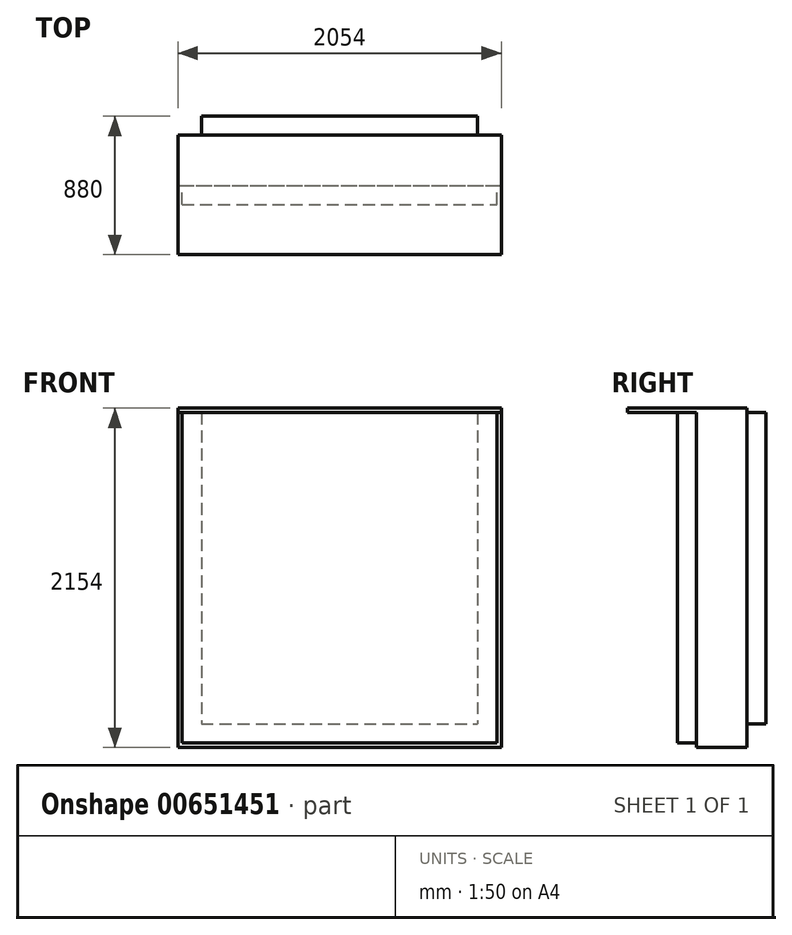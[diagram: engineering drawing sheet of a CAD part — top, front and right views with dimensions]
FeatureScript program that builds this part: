
annotation { "Feature Type Name" : "Feature", "Feature Type Description" : "" }
export const myFeature = defineFeature(function(context is Context, id is Id, definition is map)
    precondition{}
    {
        {
            var Q0;
            Q0=qCreatedBy(makeId("Front.planeOp"),FACE);
            var sketch = newSketch(context, id + "F0", { "sketchPlane" : qUnion([Q0])});
            skLineSegment(sketch, "E0.bottom", {"start": v(1935, 1905) * mm, "end": v(-1935, 1905) * mm});
            skLineSegment(sketch, "E0.top", {"start": v(1935, -1905) * mm, "end": v(-1935, -1905) * mm});
            skLineSegment(sketch, "E0.left", {"start": v(1935, 1905) * mm, "end": v(1935, -1905) * mm});
            skLineSegment(sketch, "E0.right", {"start": v(-1935, 1905) * mm, "end": v(-1935, -1905) * mm});
            skPoint(sketch, "E0.middle", {"position": v(0, 0) * mm});
            skSolve(sketch);
        }
        {
            var Q0;
            Q0=makeQuery(id+"F0.imprint","IMPRINT",FACE,{"disambiguationData":[TD([[makeQuery(id+"F0.imprint","IMPRINT",EDGE,{"derivedFrom":sQuery(id+"F0.wireOp",EDGE,"E0.bottom")}),1.0]])]});
            var sketch = newSketch(context, id + "F1", { "sketchPlane" : qUnion([Q0])});
            skLineSegment(sketch, "E1.bottom", {"start": v(-877, 1878) * mm, "end": v(877, 1878) * mm});
            skLineSegment(sketch, "E1.top", {"start": v(-877, -99) * mm, "end": v(877, -99) * mm});
            skLineSegment(sketch, "E1.left", {"start": v(-877, 1878) * mm, "end": v(-877, -99) * mm});
            skLineSegment(sketch, "E1.right", {"start": v(877, 1878) * mm, "end": v(877, -99) * mm});
            skSolve(sketch);
        }
        {
            var Q0;
            Q0=makeQuery(id+"F1.imprint","IMPRINT",FACE,{"disambiguationData":[TD([[makeQuery(id+"F1.imprint","IMPRINT",EDGE,{"derivedFrom":sQuery(id+"F1.wireOp",EDGE,"E1.bottom")}),-1.0]])]});
            extrude(context, id + "F2", {"entities" : qUnion([Q0]), "depth" : 120 * mm, "offsetDistance" : 25 * mm});
        }
        {
            var Q0;
            Q0=makeQuery(id+"F2.opExtrude","CAP_FACE",FACE,{"disambiguationData":[OSD([sQuery(id+"F1.wireOp",EDGE,"E1.bottom"),sQuery(id+"F1.wireOp",EDGE,"E1.top"),sQuery(id+"F1.wireOp",EDGE,"E1.left"),sQuery(id+"F1.wireOp",EDGE,"E1.right")])],"isStart":false});
            var sketch = newSketch(context, id + "F3", { "sketchPlane" : qUnion([Q0])});
            skLineSegment(sketch, "E2.bottom", {"start": v(-1027, 1905) * mm, "end": v(1027, 1905) * mm});
            skLineSegment(sketch, "E2.top", {"start": v(-1027, -249) * mm, "end": v(1027, -249) * mm});
            skLineSegment(sketch, "E2.left", {"start": v(-1027, 1905) * mm, "end": v(-1027, -249) * mm});
            skLineSegment(sketch, "E2.right", {"start": v(1027, 1905) * mm, "end": v(1027, -249) * mm});
            skSolve(sketch);
        }
        {
            var Q0;
            Q0=makeQuery(id+"F3.imprint","IMPRINT",FACE,{"disambiguationData":[TD([[makeQuery(id+"F3.imprint","IMPRINT",EDGE,{"derivedFrom":makeQuery(id+"F2.opExtrude","CAP_EDGE",EDGE,{"disambiguationData":[OSD([sQuery(id+"F1.wireOp",EDGE,"E1.bottom")])],"isStart":false})}),-1.0]])]});
            var Q1;
            Q1=makeQuery(id+"F3.imprint","IMPRINT",FACE,{"disambiguationData":[TD([[makeQuery(id+"F3.imprint","IMPRINT",EDGE,{"derivedFrom":sQuery(id+"F3.wireOp",EDGE,"E2.bottom")}),-1.0]])]});
            extrude(context, id + "F4", {"entities" : qUnion([Q0, Q1]), "operationType" : NewBodyOperationType.ADD, "depth" : 320 * mm, "offsetDistance" : 25 * mm});
        }
        {
            var Q0;
            Q0=makeQuery(id+"F4.opExtrude","CAP_FACE",FACE,{"disambiguationData":[OSD([sQuery(id+"F3.wireOp",EDGE,"E2.bottom"),sQuery(id+"F3.wireOp",EDGE,"E2.top"),sQuery(id+"F3.wireOp",EDGE,"E2.left"),sQuery(id+"F3.wireOp",EDGE,"E2.right")])],"isStart":false});
            var sketch = newSketch(context, id + "F5", { "sketchPlane" : qUnion([Q0])});
            skLineSegment(sketch, "E3.bottom", {"start": v(-1027, 1905) * mm, "end": v(1027, 1905) * mm});
            skLineSegment(sketch, "E3.top", {"start": v(-1027, 1878) * mm, "end": v(1027, 1878) * mm});
            skLineSegment(sketch, "E3.left", {"start": v(-1027, 1905) * mm, "end": v(-1027, 1878) * mm});
            skLineSegment(sketch, "E3.right", {"start": v(1027, 1905) * mm, "end": v(1027, 1878) * mm});
            skLineSegment(sketch, "E4.bottom", {"start": v(-1000, -222) * mm, "end": v(1000, -222) * mm});
            skLineSegment(sketch, "E4.top", {"start": v(-1000, 1878) * mm, "end": v(1000, 1878) * mm});
            skLineSegment(sketch, "E4.left", {"start": v(-1000, -222) * mm, "end": v(-1000, 1878) * mm});
            skLineSegment(sketch, "E4.right", {"start": v(1000, -222) * mm, "end": v(1000, 1878) * mm});
            skSolve(sketch);
        }
        {
            var Q0;
            Q0=makeQuery(id+"F5.imprint","IMPRINT",FACE,{"disambiguationData":[TD([[makeQuery(id+"F5.imprint","IMPRINT",EDGE,{"derivedFrom":sQuery(id+"F5.wireOp",EDGE,"E4.bottom")}),1.0]])]});
            extrude(context, id + "F6", {"entities" : qUnion([Q0]), "operationType" : NewBodyOperationType.ADD, "depth" : 120 * mm, "offsetDistance" : 25 * mm});
        }
        {
            var Q0;
            Q0=makeQuery(id+"F4.opExtrude","CAP_FACE",FACE,{"disambiguationData":[OSD([sQuery(id+"F3.wireOp",EDGE,"E2.bottom"),sQuery(id+"F3.wireOp",EDGE,"E2.top"),sQuery(id+"F3.wireOp",EDGE,"E2.left"),sQuery(id+"F3.wireOp",EDGE,"E2.right")])],"isStart":false});
            var sketch = newSketch(context, id + "F7", { "sketchPlane" : qUnion([Q0])});
            skLineSegment(sketch, "E5.bottom", {"start": v(-1027, 1905) * mm, "end": v(1027, 1905) * mm});
            skLineSegment(sketch, "E5.top", {"start": v(-1027, 1878) * mm, "end": v(1027, 1878) * mm});
            skLineSegment(sketch, "E5.left", {"start": v(-1027, 1905) * mm, "end": v(-1027, 1878) * mm});
            skLineSegment(sketch, "E5.right", {"start": v(1027, 1905) * mm, "end": v(1027, 1878) * mm});
            skSolve(sketch);
        }
        {
            var Q0;
            Q0=makeQuery(id+"F7.imprint","IMPRINT",FACE,{"disambiguationData":[TD([[makeQuery(id+"F7.imprint","IMPRINT",EDGE,{"derivedFrom":sQuery(id+"F7.wireOp",EDGE,"E5.bottom")}),-1.0]])]});
            extrude(context, id + "F8", {"entities" : qUnion([Q0]), "operationType" : NewBodyOperationType.ADD, "depth" : 440 * mm, "offsetDistance" : 25 * mm});
        }
    });
